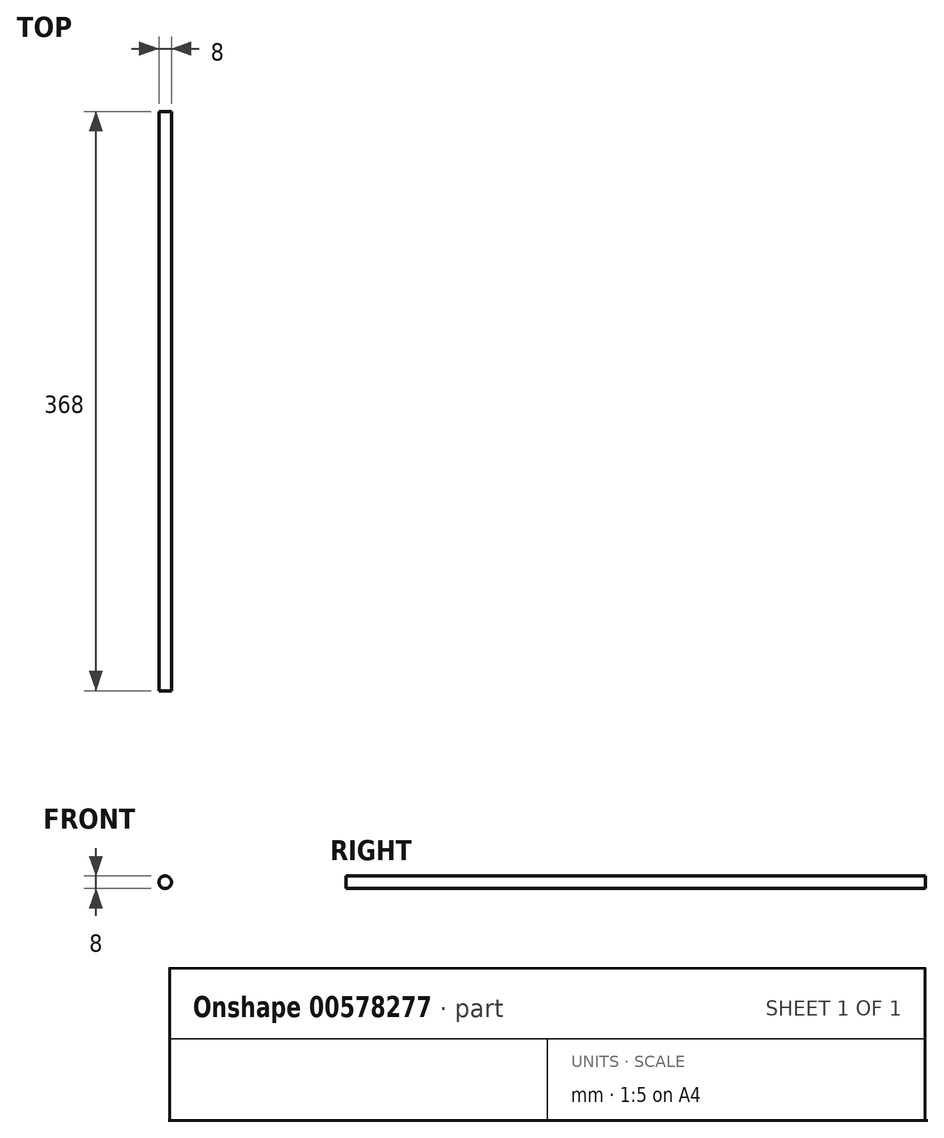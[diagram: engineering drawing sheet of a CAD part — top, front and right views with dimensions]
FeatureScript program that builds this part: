
annotation { "Feature Type Name" : "Feature", "Feature Type Description" : "" }
export const myFeature = defineFeature(function(context is Context, id is Id, definition is map)
    precondition{}
    {
        {
            var Q0;
            Q0=qCreatedBy(makeId("Front.planeOp"),FACE);
            var sketch = newSketch(context, id + "F0", { "sketchPlane" : qUnion([Q0])});
            skCircle(sketch, "E0", {"center": v(0, 0) * mm, "radius": 4 * mm});
            skSolve(sketch);
        }
        {
            var Q0;
            Q0=qSketchRegion(id+"F0",true);
            extrude(context, id + "F1", {"entities" : qUnion([Q0]), "depth" : 368 * mm, "offsetDistance" : 25 * mm});
        }
    });
